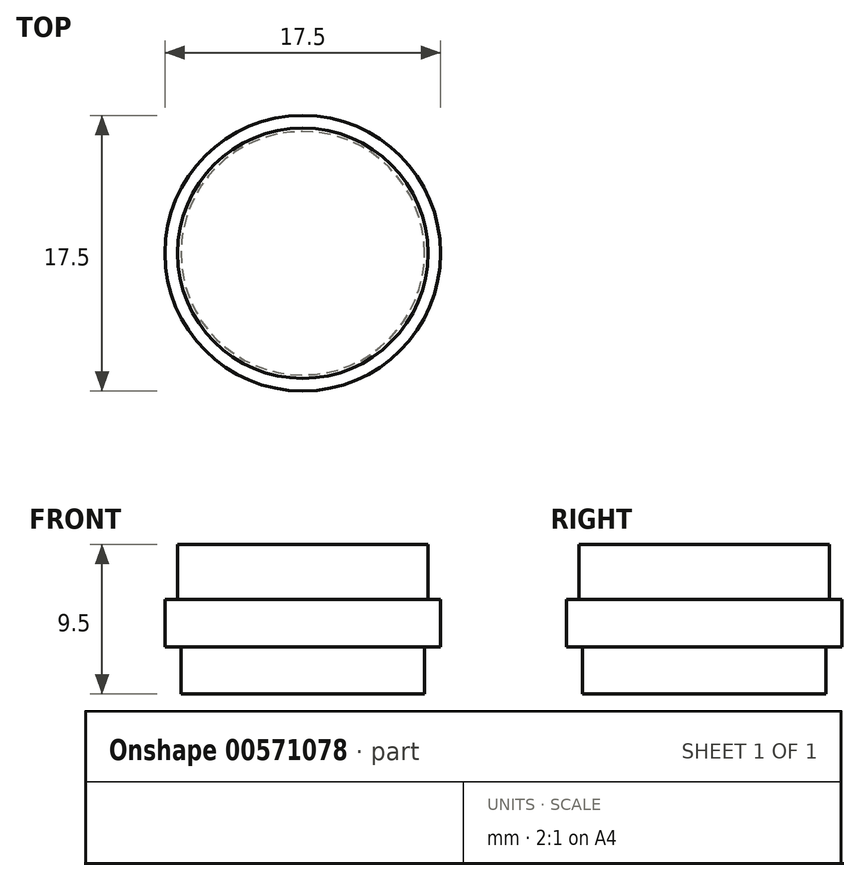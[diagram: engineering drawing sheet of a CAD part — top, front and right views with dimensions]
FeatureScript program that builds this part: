
annotation { "Feature Type Name" : "Feature", "Feature Type Description" : "" }
export const myFeature = defineFeature(function(context is Context, id is Id, definition is map)
    precondition{}
    {
        {
            var Q0;
            Q0=qCreatedBy(makeId("Top.planeOp"),FACE);
            var sketch = newSketch(context, id + "F0", { "sketchPlane" : qUnion([Q0])});
            skCircle(sketch, "E0", {"center": v(0, 0) * mm, "radius": 8.75 * mm});
            skSolve(sketch);
        }
        {
            var Q0;
            Q0 = qSketchRegion(id + "F0", true);
            extrude(context, id + "F1", {"entities" : qUnion([Q0]), "depth" : 3 * mm, "offsetDistance" : 25 * mm});
        }
        {
            var Q0;
            Q0=makeQuery(id+"F1.opExtrude","CAP_FACE",FACE,{"disambiguationData":[OSD([sQuery(id+"F0.wireOp",EDGE,"E0")])],"isStart":false});
            var sketch = newSketch(context, id + "F2", { "sketchPlane" : qUnion([Q0])});
            skCircle(sketch, "E1", {"center": v(0, 0) * mm, "radius": 7.95 * mm});
            skSolve(sketch);
        }
        {
            var Q0;
            Q0=makeQuery(id+"F2.imprint","IMPRINT",FACE,{"disambiguationData":[TD([[makeQuery(id+"F2.imprint","IMPRINT",EDGE,{"derivedFrom":sQuery(id+"F2.wireOp",EDGE,"E1")}),1.0]])]});
            extrude(context, id + "F3", {"entities" : qUnion([Q0]), "operationType" : NewBodyOperationType.ADD, "depth" : 3.5 * mm, "offsetDistance" : 25 * mm});
        }
        {
            var Q0;
            Q0=makeQuery(id+"F1.opExtrude","CAP_FACE",FACE,{"disambiguationData":[OSD([sQuery(id+"F0.wireOp",EDGE,"E0")])],"isStart":true});
            var sketch = newSketch(context, id + "F4", { "sketchPlane" : qUnion([Q0])});
            skCircle(sketch, "E2", {"center": v(0, 0) * mm, "radius": 7.73 * mm});
            skSolve(sketch);
        }
        {
            var Q0;
            Q0 = qSketchRegion(id + "F4", true);
            extrude(context, id + "F5", {"entities" : qUnion([Q0]), "operationType" : NewBodyOperationType.ADD, "depth" : 3 * mm, "offsetDistance" : 25 * mm});
        }
    });
